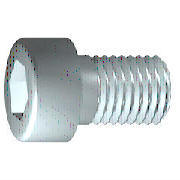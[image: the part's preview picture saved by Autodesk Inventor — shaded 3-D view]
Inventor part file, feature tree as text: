
AUTODESK INVENTOR PART (.ipt)
format: ipt  version: 2022 (Build 260153000, 153)  size: 196,608 bytes
history: native  units: mm (DEFAULTED — no unit token found)
features: sketch x2, other x1, extrude x1, plane x1, fillet x1
ambient origin geometry x7: Origin, YZ Plane, XY Plane, X Axis, Y Axis, Z Axis, Center Point
bodies: Solid1 (feature_tree)
feature tree (6):
  other  "Базовый элемент"
  extrude  "Паз"  Depth=5.0mm
  plane  "Work Plane1"
  fillet  "Fillet2"  Radius=0.24548mm
  sketch  "Эскиз1"
  sketch  "Эскиз2"
